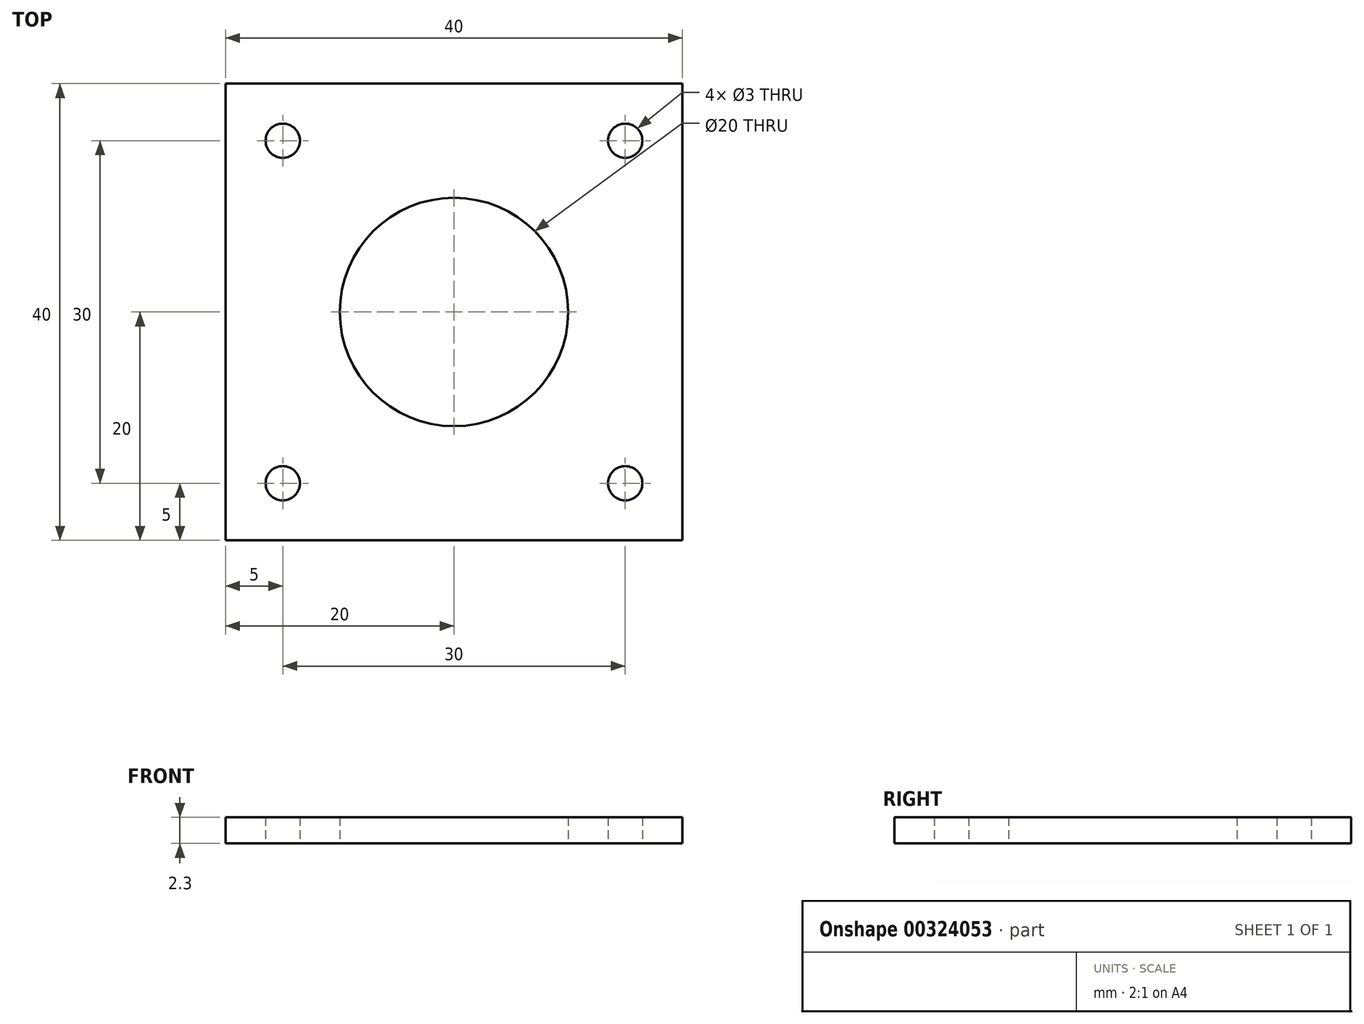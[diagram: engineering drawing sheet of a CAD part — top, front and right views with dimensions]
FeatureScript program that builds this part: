
annotation { "Feature Type Name" : "Feature", "Feature Type Description" : "" }
export const myFeature = defineFeature(function(context is Context, id is Id, definition is map)
    precondition{}
    {
        {
            var Q0;
            Q0=qCreatedBy(makeId("Top.planeOp"),FACE);
            var sketch = newSketch(context, id + "F0", { "sketchPlane" : qUnion([Q0])});
            skLineSegment(sketch, "E0.bottom", {"start": v(-20, 20) * mm, "end": v(20, 20) * mm});
            skLineSegment(sketch, "E0.top", {"start": v(-20, -20) * mm, "end": v(20, -20) * mm});
            skLineSegment(sketch, "E0.left", {"start": v(-20, 20) * mm, "end": v(-20, -20) * mm});
            skLineSegment(sketch, "E0.right", {"start": v(20, 20) * mm, "end": v(20, -20) * mm});
            skCircle(sketch, "E1", {"center": v(0, 0) * mm, "radius": 10 * mm});
            skCircle(sketch, "E2", {"center": v(-15, 15) * mm, "radius": 1.5 * mm});
            skCircle(sketch, "E3", {"center": v(15, 15) * mm, "radius": 1.5 * mm});
            skCircle(sketch, "E4", {"center": v(15, -15) * mm, "radius": 1.5 * mm});
            skCircle(sketch, "E5", {"center": v(-15, -15) * mm, "radius": 1.5 * mm});
            skSolve(sketch);
        }
        {
            var Q0;
            Q0=makeQuery(id+"F0.imprint","IMPRINT",FACE,{"disambiguationData":[TD([[makeQuery(id+"F0.imprint","IMPRINT",EDGE,{"derivedFrom":sQuery(id+"F0.wireOp",EDGE,"E0.bottom")}),-1.0]])]});
            extrude(context, id + "F1", {"entities" : qUnion([Q0]), "depth" : 2.3 * mm});
        }
    });
